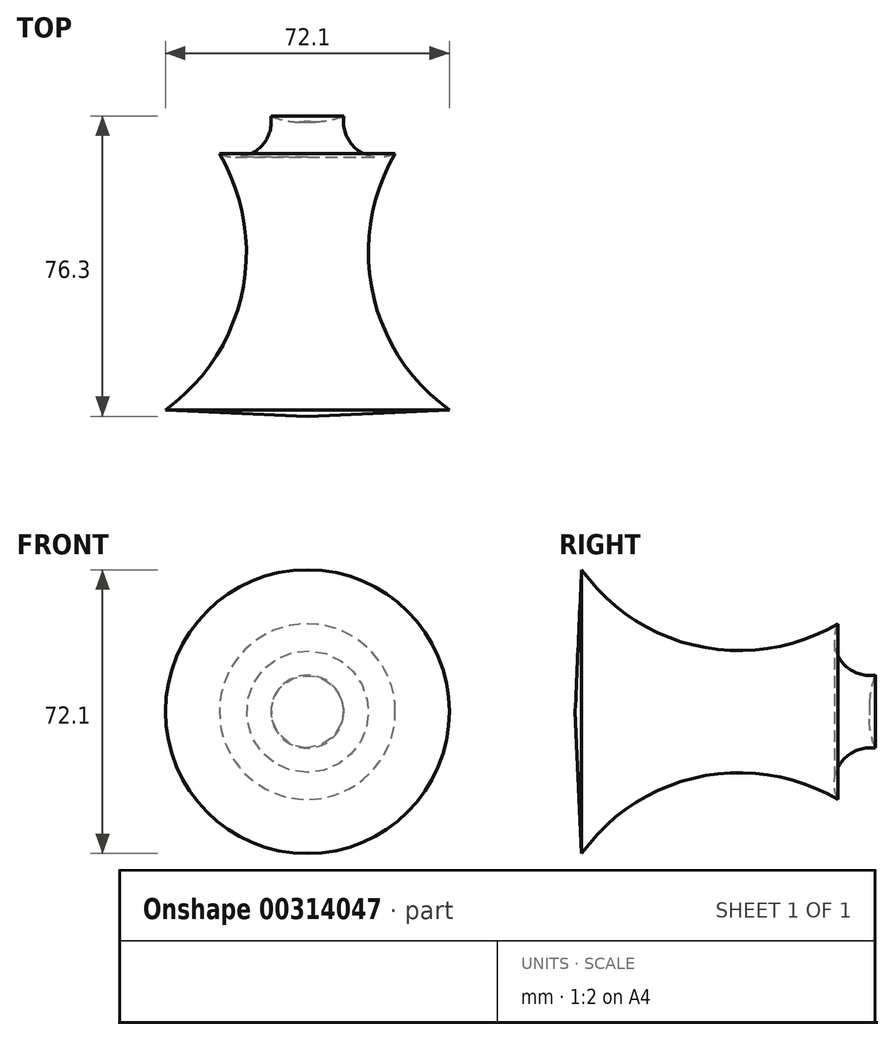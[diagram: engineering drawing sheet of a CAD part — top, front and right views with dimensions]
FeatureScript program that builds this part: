
annotation { "Feature Type Name" : "Feature", "Feature Type Description" : "" }
export const myFeature = defineFeature(function(context is Context, id is Id, definition is map)
    precondition{}
    {
        {
            var Q0;
            Q0=qCreatedBy(makeId("Top.planeOp"),FACE);
            var sketch = newSketch(context, id + "F0", { "sketchPlane" : qUnion([Q0])});
            skLineSegment(sketch, "E0", {"start": v(0, -57.45) * mm, "end": v(0, 51.63) * mm});
            skArc(sketch, "E1", {"start": v(0, 17.44) * mm, "mid": v(19.37, 34.54) * mm, "end": v(0, 51.63) * mm});
            skArc(sketch, "E2", {"start": v(9.27, 18.85) * mm, "mid": v(12.9, 10.11) * mm, "end": v(22.33, 9.3) * mm});
            skArc(sketch, "E3", {"start": v(22.33, 9.3) * mm, "mid": v(16.56, -25.92) * mm, "end": v(36.05, -55.82) * mm});
            skLineSegment(sketch, "E4", {"start": v(36.05, -55.82) * mm, "end": v(0, -57.45) * mm});
            skSolve(sketch);
        }
        {
            var Q0;
            Q0 = qSketchRegion(id + "F0", true);
            var Q1;
            Q1=sQuery(id+"F0.wireOp",EDGE,"E0");
            revolve(context, id + "F1", {"entities" : qUnion([Q0]), "axis" : qUnion([Q1]), "revolveType" : RevolveType.FULL});
        }
    });
